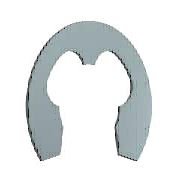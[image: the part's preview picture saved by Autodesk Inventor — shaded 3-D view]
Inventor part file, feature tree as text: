
AUTODESK INVENTOR PART (.ipt)
format: ipt  version: 2020.2 (Build 242310000, 310)  size: 157,184 bytes
history: native  units: mm (DEFAULTED — no unit token found)
features: other x2, plane x1
ambient origin geometry x8: Origin, YZ Plane, XZ Plane, XY Plane, X Axis, Y Axis, Z Axis, Center Point
bodies: Solid1 (feature_tree), Body (feature_tree)
feature tree (3):
  other  "Work Axis1"
  other  "Work Axis2"
  plane  "Work Plane1"
